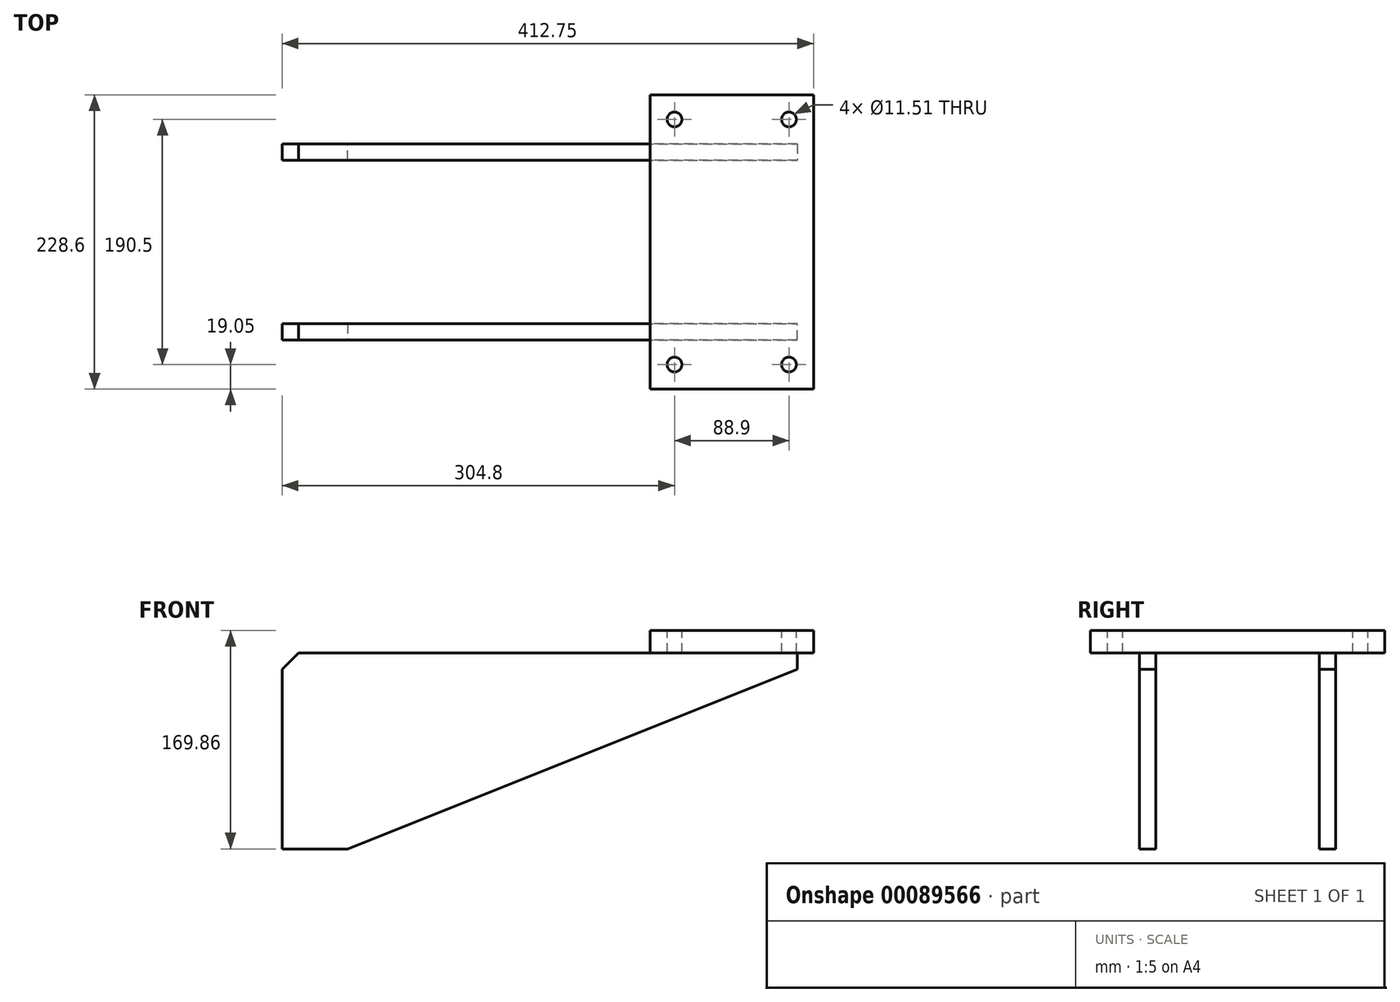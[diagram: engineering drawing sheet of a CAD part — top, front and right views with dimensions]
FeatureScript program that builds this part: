
annotation { "Feature Type Name" : "Feature", "Feature Type Description" : "" }
export const myFeature = defineFeature(function(context is Context, id is Id, definition is map)
    precondition{}
    {
        {
            var Q0;
            Q0=qCreatedBy(makeId("Top.planeOp"),FACE);
            var sketch = newSketch(context, id + "F0", { "sketchPlane" : qUnion([Q0])});
            skLineSegment(sketch, "E0.bottom", {"start": v(-63.5, 114.3) * mm, "end": v(63.5, 114.3) * mm});
            skLineSegment(sketch, "E0.top", {"start": v(-63.5, -114.3) * mm, "end": v(63.5, -114.3) * mm});
            skLineSegment(sketch, "E0.left", {"start": v(-63.5, 114.3) * mm, "end": v(-63.5, -114.3) * mm});
            skLineSegment(sketch, "E0.right", {"start": v(63.5, 114.3) * mm, "end": v(63.5, -114.3) * mm});
            skPoint(sketch, "E0.middle", {"position": v(0, 0) * mm});
            skSolve(sketch);
        }
        {
            var Q0;
            Q0 = qSketchRegion(id + "F0", true);
            extrude(context, id + "F1", {"entities" : qUnion([Q0]), "depth" : 17.46 * mm});
        }
        {
            var Q0;
            Q0=makeQuery(id+"F1.opExtrude","CAP_FACE",FACE,{"disambiguationData":[OSD([sQuery(id+"F0.wireOp",EDGE,"E0.bottom"),sQuery(id+"F0.wireOp",EDGE,"E0.top"),sQuery(id+"F0.wireOp",EDGE,"E0.left"),sQuery(id+"F0.wireOp",EDGE,"E0.right")])],"isStart":false});
            var sketch = newSketch(context, id + "F2", { "sketchPlane" : qUnion([Q0])});
            skLineSegment(sketch, "E1", {"start": v(0, 114.3) * mm, "end": v(0, -114.3) * mm, "construction": true});
            skLineSegment(sketch, "E2", {"start": v(-63.5, 0) * mm, "end": v(63.5, 0) * mm, "construction": true});
            skLineSegment(sketch, "E3.0", {"start": v(-44.45, 114.3) * mm, "end": v(-44.45, -114.3) * mm, "construction": true});
            skLineSegment(sketch, "E4.0", {"start": v(-63.5, 95.25) * mm, "end": v(63.5, 95.25) * mm, "construction": true});
            skPoint(sketch, "E5", {"position": v(-44.45, 95.25) * mm});
            skPoint(sketch, "E6.0.1.0", {"position": v(-44.45, -95.25) * mm});
            skPoint(sketch, "E6.1.0.0", {"position": v(44.45, 95.25) * mm});
            skPoint(sketch, "E6.1.1.0", {"position": v(44.45, -95.25) * mm});
            skLineSegment(sketch, "E6.direction1", {"start": v(-44.45, 95.25) * mm, "end": v(44.45, 95.25) * mm, "construction": true});
            skLineSegment(sketch, "E6.direction2", {"start": v(-44.45, 95.25) * mm, "end": v(-44.45, -95.25) * mm, "construction": true});
            skSolve(sketch);
        }
        {
            var Q0;
            Q0=sQuery(id+"F2.wireOp",VERTEX,"E5");
            var Q1;
            Q1=sQuery(id+"F2.wireOp",VERTEX,"E6.1.0.0");
            var Q2;
            Q2=sQuery(id+"F2.wireOp",VERTEX,"E6.1.1.0");
            var Q3;
            Q3=sQuery(id+"F2.wireOp",VERTEX,"E6.0.1.0");
            var Q4;
            Q4=makeQuery(id+"F1.opExtrude","SWEPT_BODY",BODY,{"disambiguationData":[OSD([sQuery(id+"F0.wireOp",EDGE,"E0.bottom"),sQuery(id+"F0.wireOp",EDGE,"E0.top"),sQuery(id+"F0.wireOp",EDGE,"E0.left"),sQuery(id+"F0.wireOp",EDGE,"E0.right")])]});
            hole(context, id + "F3", {"style" : HoleStyle.SIMPLE, "endStyle" : HoleEndStyle.THROUGH, "standardTappedOrClearance" : lookupTablePath({ "standard" : "ANSI", "engagement" : "75%", "pitch" : "20 tpi", "size" : "1/2", "type" : "Tapped" }), "standardBlindInLast" : lookupTablePath({ "standard" : "ANSI", "engagement" : "75%", "pitch" : "20 tpi", "size" : "1/2", "type" : "Tapped" }), "holeDiameter" : 11.5 * mm, "locations" : qUnion([Q0, Q1, Q2, Q3]), "scope" : qUnion([Q4]), "isTappedThrough" : true, "majorDiameter" : 12.7 * mm, "showTappedDepth" : true});
        }
        {
            var Q0;
            Q0=makeQuery(id+"F1.opExtrude","CAP_FACE",FACE,{"disambiguationData":[OSD([sQuery(id+"F0.wireOp",EDGE,"E0.bottom"),sQuery(id+"F0.wireOp",EDGE,"E0.top"),sQuery(id+"F0.wireOp",EDGE,"E0.left"),sQuery(id+"F0.wireOp",EDGE,"E0.right")])],"isStart":true});
            var sketch = newSketch(context, id + "F4", { "sketchPlane" : qUnion([Q0])});
            skLineSegment(sketch, "E7.0", {"start": v(63.5, -114.3) * mm, "end": v(63.5, 114.3) * mm, "construction": true});
            skLineSegment(sketch, "E8.0", {"start": v(50.8, -76.2) * mm, "end": v(50.8, -63.5) * mm});
            skLineSegment(sketch, "E9.0", {"start": v(-349.25, -76.2) * mm, "end": v(-349.25, -63.5) * mm});
            skLineSegment(sketch, "E10", {"start": v(144.03, 0) * mm, "end": v(-401.25, 0) * mm, "construction": true});
            skPoint(sketch, "E10.endSnap0", {"position": v(-63.5, 0) * mm});
            skLineSegment(sketch, "E11.0", {"start": v(50.8, -63.5) * mm, "end": v(-349.25, -63.5) * mm});
            skLineSegment(sketch, "E12.0", {"start": v(50.8, -76.2) * mm, "end": v(-349.25, -76.2) * mm});
            skSolve(sketch);
        }
        {
            var Q0;
            Q0 = qSketchRegion(id + "F4", true);
            extrude(context, id + "F5", {"entities" : qUnion([Q0]), "depth" : 152.4 * mm});
        }
        {
            var Q0;
            Q0=makeQuery(id+"F5.opExtrude","SWEPT_FACE",FACE,{"disambiguationData":[OSD([sQuery(id+"F4.wireOp",EDGE,"E12.0")])]});
            var sketch = newSketch(context, id + "F6", { "sketchPlane" : qUnion([Q0])});
            skLineSegment(sketch, "E13.0", {"start": v(349.25, -152.4) * mm, "end": v(349.25, 0) * mm, "construction": true});
            skLineSegment(sketch, "E14.0", {"start": v(-50.8, 0) * mm, "end": v(349.25, 0) * mm, "construction": true});
            skLineSegment(sketch, "E15.0", {"start": v(-50.8, -12.7) * mm, "end": v(349.25, -12.7) * mm, "construction": true});
            skLineSegment(sketch, "E16.0", {"start": v(298.45, -152.4) * mm, "end": v(298.45, 0) * mm, "construction": true});
            skLineSegment(sketch, "E17.0", {"start": v(342.9, -6.35) * mm, "end": v(-44.45, -6.35) * mm, "construction": true});
            skLineSegment(sketch, "E17.1", {"start": v(342.9, -146.05) * mm, "end": v(342.9, -6.35) * mm, "construction": true});
            skLineSegment(sketch, "E17.2", {"start": v(-44.45, -146.05) * mm, "end": v(342.9, -146.05) * mm, "construction": true});
            skLineSegment(sketch, "E17.3", {"start": v(-44.45, -6.35) * mm, "end": v(-44.45, -146.05) * mm, "construction": true});
            skLineSegment(sketch, "E18.0", {"start": v(-50.8, -152.4) * mm, "end": v(349.25, -152.4) * mm});
            skLineSegment(sketch, "E19.0", {"start": v(-50.8, -152.4) * mm, "end": v(-50.8, 0) * mm});
            skLineSegment(sketch, "E20", {"start": v(298.45, -152.4) * mm, "end": v(-50.8, -12.7) * mm});
            skSolve(sketch);
        }
        {
            var Q0;
            Q0 = qSketchRegion(id + "F6", true);
            extrude(context, id + "F7", {"entities" : qUnion([Q0]), "operationType" : NewBodyOperationType.REMOVE, "endBound" : BoundingType.THROUGH_ALL, "oppositeDirection" : true, "depth" : 25.4 * mm});
        }
        {
            var Q0;
            Q0=makeQuery(id+"F5.opExtrude","CAP_EDGE",EDGE,{"disambiguationData":[OSD([sQuery(id+"F4.wireOp",EDGE,"E9.0")])],"isStart":true});
            chamfer(context, id + "F8", {"entities" : qUnion([Q0]), "width" : 12.7 * mm, "tangentPropagation" : true});
        }
        {
            var Q0;
            Q0=makeQuery(id+"F5.opExtrude","SWEPT_BODY",BODY,{"disambiguationData":[OSD([sQuery(id+"F4.wireOp",EDGE,"E8.0"),sQuery(id+"F4.wireOp",EDGE,"E9.0"),sQuery(id+"F4.wireOp",EDGE,"E11.0"),sQuery(id+"F4.wireOp",EDGE,"E12.0")])]});
            var Q1;
            Q1=qCreatedBy(makeId("Front.planeOp"),FACE);
            mirror(context, id + "F9", {"operationType" : NewBodyOperationType.ADD, "entities" : qUnion([Q0]), "mirrorPlane" : qUnion([Q1])});
        }
    });
